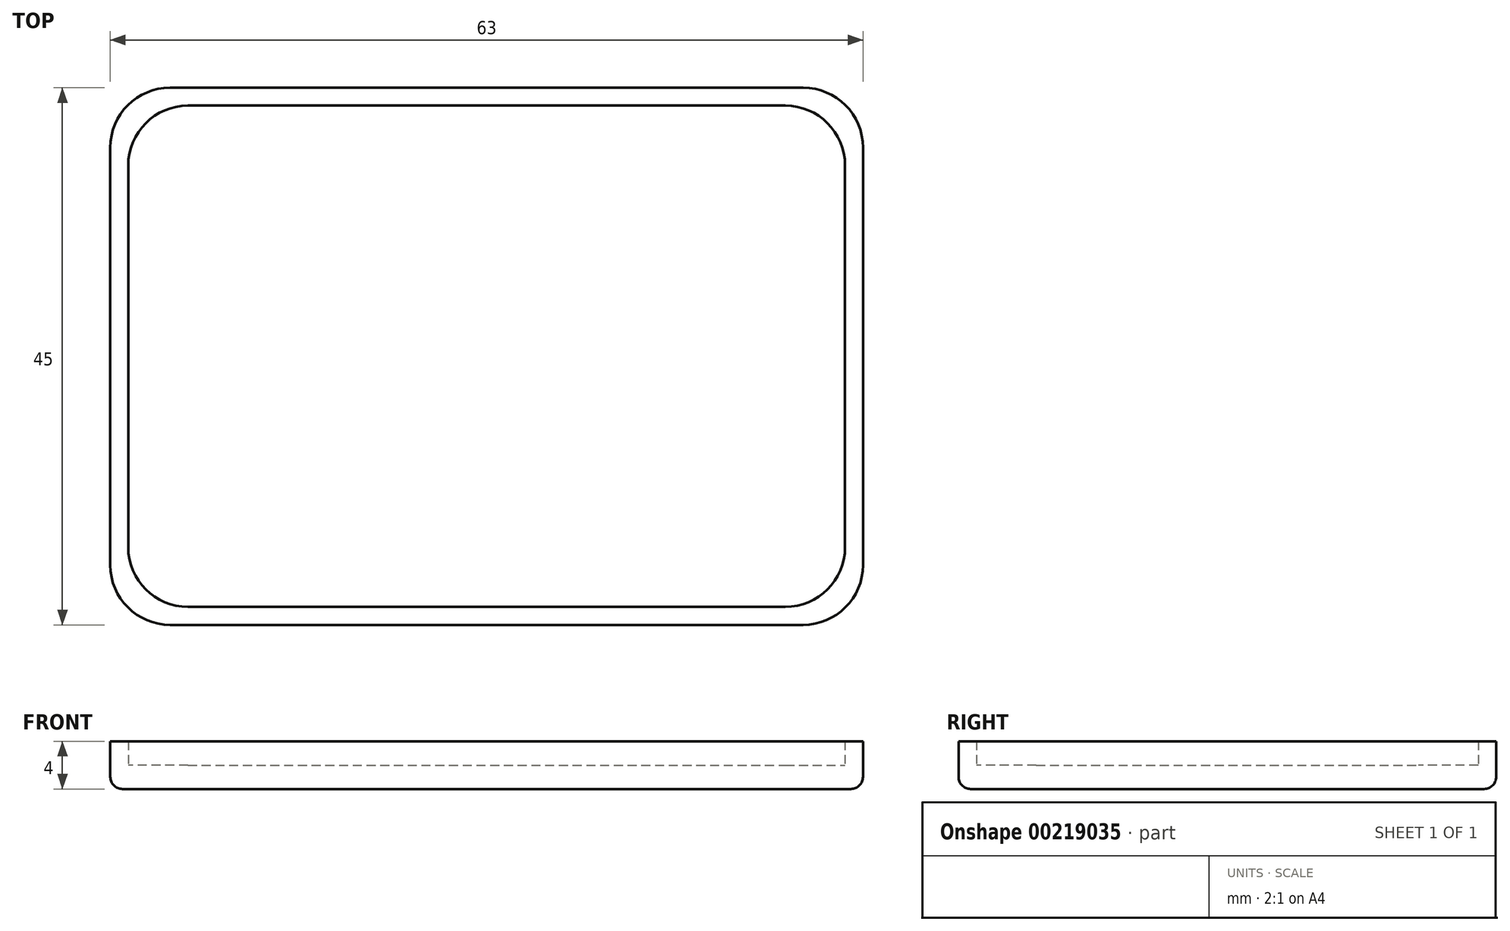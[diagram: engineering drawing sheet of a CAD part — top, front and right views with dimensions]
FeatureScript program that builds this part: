
annotation { "Feature Type Name" : "Feature", "Feature Type Description" : "" }
export const myFeature = defineFeature(function(context is Context, id is Id, definition is map)
    precondition{}
    {
        {
            var Q0;
            Q0=qCreatedBy(makeId("Top.planeOp"),FACE);
            var sketch = newSketch(context, id + "F0", { "sketchPlane" : qUnion([Q0])});
            skLineSegment(sketch, "E0.bottom", {"start": v(0, 0) * mm, "end": v(60, 0) * mm});
            skLineSegment(sketch, "E0.top", {"start": v(0, 42) * mm, "end": v(60, 42) * mm});
            skLineSegment(sketch, "E0.left", {"start": v(0, 0) * mm, "end": v(0, 42) * mm});
            skLineSegment(sketch, "E0.right", {"start": v(60, 0) * mm, "end": v(60, 42) * mm});
            skSolve(sketch);
        }
        {
            var Q0;
            Q0=qSketchRegion(id+"F0",true);
            extrude(context, id + "F1", {"entities" : qUnion([Q0]), "depth" : 2 * mm});
        }
        {
            var Q0;
            Q0=qCreatedBy(makeId("Top.planeOp"),FACE);
            var sketch = newSketch(context, id + "F2", { "sketchPlane" : qUnion([Q0])});
            skLineSegment(sketch, "E1.bottom", {"start": v(-1.5, 43.5) * mm, "end": v(61.5, 43.5) * mm});
            skLineSegment(sketch, "E1.top", {"start": v(-1.5, -1.5) * mm, "end": v(61.5, -1.5) * mm});
            skLineSegment(sketch, "E1.left", {"start": v(-1.5, 43.5) * mm, "end": v(-1.5, -1.5) * mm});
            skLineSegment(sketch, "E1.right", {"start": v(61.5, 43.5) * mm, "end": v(61.5, -1.5) * mm});
            skLineSegment(sketch, "E2.bottom", {"start": v(0, 42) * mm, "end": v(60, 42) * mm});
            skLineSegment(sketch, "E2.top", {"start": v(0, 0) * mm, "end": v(60, 0) * mm});
            skLineSegment(sketch, "E2.left", {"start": v(0, 42) * mm, "end": v(0, 0) * mm});
            skLineSegment(sketch, "E2.right", {"start": v(60, 42) * mm, "end": v(60, 0) * mm});
            skLineSegment(sketch, "E3", {"start": v(30, 42) * mm, "end": v(30, 43.5) * mm, "construction": true});
            skLineSegment(sketch, "E4", {"start": v(0, 21) * mm, "end": v(-1.5, 21) * mm, "construction": true});
            skSolve(sketch);
        }
        {
            var Q0;
            Q0=qSketchRegion(id+"F2",true);
            var Q1;
            Q1=qConstructionFilter(qBodyType(qCreatedBy(id+"F2",EDGE),BodyType.WIRE),ConstructionObject.NO);
            extrude(context, id + "F3", {"entities" : qUnion([Q0]), "operationType" : NewBodyOperationType.ADD, "surfaceEntities" : qUnion([Q1]), "depth" : 4 * mm});
        }
        {
            var Q0;
            Q0=makeQuery(id+"F3.opExtrude","SWEPT_EDGE",EDGE,{"disambiguationData":[OSD([sQuery(id+"F2.wireOp",EDGE,"E1.top"),sQuery(id+"F2.wireOp",EDGE,"E1.left")])]});
            var Q1;
            Q1=makeQuery(id+"F3.opExtrude","SWEPT_EDGE",EDGE,{"disambiguationData":[OSD([sQuery(id+"F2.wireOp",EDGE,"E1.top"),sQuery(id+"F2.wireOp",EDGE,"E1.right")])]});
            var Q2;
            Q2=makeQuery(id+"F3.opExtrude","SWEPT_EDGE",EDGE,{"disambiguationData":[OSD([sQuery(id+"F2.wireOp",EDGE,"E1.bottom"),sQuery(id+"F2.wireOp",EDGE,"E1.left")])]});
            var Q3;
            Q3=makeQuery(id+"F3.opExtrude","SWEPT_EDGE",EDGE,{"disambiguationData":[OSD([sQuery(id+"F2.wireOp",EDGE,"E2.bottom"),sQuery(id+"F2.wireOp",EDGE,"E2.right")])]});
            var Q4;
            Q4=makeQuery(id+"F3.opExtrude","SWEPT_EDGE",EDGE,{"disambiguationData":[OSD([sQuery(id+"F2.wireOp",EDGE,"E1.bottom"),sQuery(id+"F2.wireOp",EDGE,"E1.right")])]});
            var Q5;
            Q5=makeQuery(id+"F3.opExtrude","SWEPT_EDGE",EDGE,{"disambiguationData":[OSD([sQuery(id+"F2.wireOp",EDGE,"E2.top"),sQuery(id+"F2.wireOp",EDGE,"E2.right")])]});
            var Q6;
            Q6=makeQuery(id+"F3.opExtrude","SWEPT_EDGE",EDGE,{"disambiguationData":[OSD([sQuery(id+"F2.wireOp",EDGE,"E2.top"),sQuery(id+"F2.wireOp",EDGE,"E2.left")])]});
            var Q7;
            Q7=makeQuery(id+"F3.opExtrude","SWEPT_EDGE",EDGE,{"disambiguationData":[OSD([sQuery(id+"F2.wireOp",EDGE,"E2.bottom"),sQuery(id+"F2.wireOp",EDGE,"E2.left")])]});
            fillet(context, id + "F4", {"entities" : qUnion([Q0, Q1, Q2, Q3, Q4, Q5, Q6, Q7]), "radius" : 5 * mm, "tangentPropagation" : true, "allowEdgeOverflow" : false});
        }
        {
            var Q0;
            Q0=makeQuery(id+"F3.opExtrude","CAP_EDGE",EDGE,{"disambiguationData":[OSD([sQuery(id+"F2.wireOp",EDGE,"E1.top")])],"isStart":true});
            var Q1;
            {var subQ0=sQuery(id+"F2.wireOp",EDGE,"E1.right");var subQ1=sQuery(id+"F2.wireOp",EDGE,"E1.top");Q1=makeQuery(id+"F4.opFillet","BLEND_EDGE",EDGE,{"blendedFrom":[makeQuery(id+"F3.opExtrude","SWEPT_EDGE",EDGE,{"disambiguationData":[OSD([subQ1,subQ0])]}),makeQuery(id+"F3.boolean.opBoolean","MERGE",FACE,{"derivedFrom":[makeQuery(id+"F1.opExtrude","CAP_FACE",FACE,{"disambiguationData":[OSD([sQuery(id+"F0.wireOp",EDGE,"E0.bottom"),sQuery(id+"F0.wireOp",EDGE,"E0.top"),sQuery(id+"F0.wireOp",EDGE,"E0.left"),sQuery(id+"F0.wireOp",EDGE,"E0.right")])],"isStart":true}),makeQuery(id+"F3.opExtrude","CAP_FACE",FACE,{"disambiguationData":[OSD([sQuery(id+"F2.wireOp",EDGE,"E1.bottom"),subQ1,sQuery(id+"F2.wireOp",EDGE,"E1.left"),subQ0,sQuery(id+"F2.wireOp",EDGE,"E2.bottom"),sQuery(id+"F2.wireOp",EDGE,"E2.top"),sQuery(id+"F2.wireOp",EDGE,"E2.left"),sQuery(id+"F2.wireOp",EDGE,"E2.right")])],"isStart":true})]})],"blendedInto":[makeQuery(id+"F3.boolean.opBoolean","MERGE",FACE,{"derivedFrom":[makeQuery(id+"F1.opExtrude","CAP_FACE",FACE,{"disambiguationData":[OSD([sQuery(id+"F0.wireOp",EDGE,"E0.bottom"),sQuery(id+"F0.wireOp",EDGE,"E0.top"),sQuery(id+"F0.wireOp",EDGE,"E0.left"),sQuery(id+"F0.wireOp",EDGE,"E0.right")])],"isStart":true}),makeQuery(id+"F3.opExtrude","CAP_FACE",FACE,{"disambiguationData":[OSD([sQuery(id+"F2.wireOp",EDGE,"E1.bottom"),subQ1,sQuery(id+"F2.wireOp",EDGE,"E1.left"),subQ0,sQuery(id+"F2.wireOp",EDGE,"E2.bottom"),sQuery(id+"F2.wireOp",EDGE,"E2.top"),sQuery(id+"F2.wireOp",EDGE,"E2.left"),sQuery(id+"F2.wireOp",EDGE,"E2.right")])],"isStart":true})]})]});}
            var Q2;
            Q2=makeQuery(id+"F3.opExtrude","CAP_EDGE",EDGE,{"disambiguationData":[OSD([sQuery(id+"F2.wireOp",EDGE,"E1.right")])],"isStart":true});
            var Q3;
            {var subQ0=sQuery(id+"F2.wireOp",EDGE,"E1.right");var subQ1=sQuery(id+"F2.wireOp",EDGE,"E1.bottom");Q3=makeQuery(id+"F4.opFillet","BLEND_EDGE",EDGE,{"blendedFrom":[makeQuery(id+"F3.opExtrude","SWEPT_EDGE",EDGE,{"disambiguationData":[OSD([subQ1,subQ0])]}),makeQuery(id+"F3.boolean.opBoolean","MERGE",FACE,{"derivedFrom":[makeQuery(id+"F1.opExtrude","CAP_FACE",FACE,{"disambiguationData":[OSD([sQuery(id+"F0.wireOp",EDGE,"E0.bottom"),sQuery(id+"F0.wireOp",EDGE,"E0.top"),sQuery(id+"F0.wireOp",EDGE,"E0.left"),sQuery(id+"F0.wireOp",EDGE,"E0.right")])],"isStart":true}),makeQuery(id+"F3.opExtrude","CAP_FACE",FACE,{"disambiguationData":[OSD([subQ1,sQuery(id+"F2.wireOp",EDGE,"E1.top"),sQuery(id+"F2.wireOp",EDGE,"E1.left"),subQ0,sQuery(id+"F2.wireOp",EDGE,"E2.bottom"),sQuery(id+"F2.wireOp",EDGE,"E2.top"),sQuery(id+"F2.wireOp",EDGE,"E2.left"),sQuery(id+"F2.wireOp",EDGE,"E2.right")])],"isStart":true})]})],"blendedInto":[makeQuery(id+"F3.boolean.opBoolean","MERGE",FACE,{"derivedFrom":[makeQuery(id+"F1.opExtrude","CAP_FACE",FACE,{"disambiguationData":[OSD([sQuery(id+"F0.wireOp",EDGE,"E0.bottom"),sQuery(id+"F0.wireOp",EDGE,"E0.top"),sQuery(id+"F0.wireOp",EDGE,"E0.left"),sQuery(id+"F0.wireOp",EDGE,"E0.right")])],"isStart":true}),makeQuery(id+"F3.opExtrude","CAP_FACE",FACE,{"disambiguationData":[OSD([subQ1,sQuery(id+"F2.wireOp",EDGE,"E1.top"),sQuery(id+"F2.wireOp",EDGE,"E1.left"),subQ0,sQuery(id+"F2.wireOp",EDGE,"E2.bottom"),sQuery(id+"F2.wireOp",EDGE,"E2.top"),sQuery(id+"F2.wireOp",EDGE,"E2.left"),sQuery(id+"F2.wireOp",EDGE,"E2.right")])],"isStart":true})]})]});}
            var Q4;
            Q4=makeQuery(id+"F3.opExtrude","CAP_EDGE",EDGE,{"disambiguationData":[OSD([sQuery(id+"F2.wireOp",EDGE,"E1.bottom")])],"isStart":true});
            var Q5;
            {var subQ0=sQuery(id+"F2.wireOp",EDGE,"E1.left");var subQ1=sQuery(id+"F2.wireOp",EDGE,"E1.bottom");Q5=makeQuery(id+"F4.opFillet","BLEND_EDGE",EDGE,{"blendedFrom":[makeQuery(id+"F3.opExtrude","SWEPT_EDGE",EDGE,{"disambiguationData":[OSD([subQ1,subQ0])]}),makeQuery(id+"F3.boolean.opBoolean","MERGE",FACE,{"derivedFrom":[makeQuery(id+"F1.opExtrude","CAP_FACE",FACE,{"disambiguationData":[OSD([sQuery(id+"F0.wireOp",EDGE,"E0.bottom"),sQuery(id+"F0.wireOp",EDGE,"E0.top"),sQuery(id+"F0.wireOp",EDGE,"E0.left"),sQuery(id+"F0.wireOp",EDGE,"E0.right")])],"isStart":true}),makeQuery(id+"F3.opExtrude","CAP_FACE",FACE,{"disambiguationData":[OSD([subQ1,sQuery(id+"F2.wireOp",EDGE,"E1.top"),subQ0,sQuery(id+"F2.wireOp",EDGE,"E1.right"),sQuery(id+"F2.wireOp",EDGE,"E2.bottom"),sQuery(id+"F2.wireOp",EDGE,"E2.top"),sQuery(id+"F2.wireOp",EDGE,"E2.left"),sQuery(id+"F2.wireOp",EDGE,"E2.right")])],"isStart":true})]})],"blendedInto":[makeQuery(id+"F3.boolean.opBoolean","MERGE",FACE,{"derivedFrom":[makeQuery(id+"F1.opExtrude","CAP_FACE",FACE,{"disambiguationData":[OSD([sQuery(id+"F0.wireOp",EDGE,"E0.bottom"),sQuery(id+"F0.wireOp",EDGE,"E0.top"),sQuery(id+"F0.wireOp",EDGE,"E0.left"),sQuery(id+"F0.wireOp",EDGE,"E0.right")])],"isStart":true}),makeQuery(id+"F3.opExtrude","CAP_FACE",FACE,{"disambiguationData":[OSD([subQ1,sQuery(id+"F2.wireOp",EDGE,"E1.top"),subQ0,sQuery(id+"F2.wireOp",EDGE,"E1.right"),sQuery(id+"F2.wireOp",EDGE,"E2.bottom"),sQuery(id+"F2.wireOp",EDGE,"E2.top"),sQuery(id+"F2.wireOp",EDGE,"E2.left"),sQuery(id+"F2.wireOp",EDGE,"E2.right")])],"isStart":true})]})]});}
            var Q6;
            Q6=makeQuery(id+"F3.opExtrude","CAP_EDGE",EDGE,{"disambiguationData":[OSD([sQuery(id+"F2.wireOp",EDGE,"E1.left")])],"isStart":true});
            var Q7;
            {var subQ0=sQuery(id+"F2.wireOp",EDGE,"E1.left");var subQ1=sQuery(id+"F2.wireOp",EDGE,"E1.top");Q7=makeQuery(id+"F4.opFillet","BLEND_EDGE",EDGE,{"blendedFrom":[makeQuery(id+"F3.opExtrude","SWEPT_EDGE",EDGE,{"disambiguationData":[OSD([subQ1,subQ0])]}),makeQuery(id+"F3.boolean.opBoolean","MERGE",FACE,{"derivedFrom":[makeQuery(id+"F1.opExtrude","CAP_FACE",FACE,{"disambiguationData":[OSD([sQuery(id+"F0.wireOp",EDGE,"E0.bottom"),sQuery(id+"F0.wireOp",EDGE,"E0.top"),sQuery(id+"F0.wireOp",EDGE,"E0.left"),sQuery(id+"F0.wireOp",EDGE,"E0.right")])],"isStart":true}),makeQuery(id+"F3.opExtrude","CAP_FACE",FACE,{"disambiguationData":[OSD([sQuery(id+"F2.wireOp",EDGE,"E1.bottom"),subQ1,subQ0,sQuery(id+"F2.wireOp",EDGE,"E1.right"),sQuery(id+"F2.wireOp",EDGE,"E2.bottom"),sQuery(id+"F2.wireOp",EDGE,"E2.top"),sQuery(id+"F2.wireOp",EDGE,"E2.left"),sQuery(id+"F2.wireOp",EDGE,"E2.right")])],"isStart":true})]})],"blendedInto":[makeQuery(id+"F3.boolean.opBoolean","MERGE",FACE,{"derivedFrom":[makeQuery(id+"F1.opExtrude","CAP_FACE",FACE,{"disambiguationData":[OSD([sQuery(id+"F0.wireOp",EDGE,"E0.bottom"),sQuery(id+"F0.wireOp",EDGE,"E0.top"),sQuery(id+"F0.wireOp",EDGE,"E0.left"),sQuery(id+"F0.wireOp",EDGE,"E0.right")])],"isStart":true}),makeQuery(id+"F3.opExtrude","CAP_FACE",FACE,{"disambiguationData":[OSD([sQuery(id+"F2.wireOp",EDGE,"E1.bottom"),subQ1,subQ0,sQuery(id+"F2.wireOp",EDGE,"E1.right"),sQuery(id+"F2.wireOp",EDGE,"E2.bottom"),sQuery(id+"F2.wireOp",EDGE,"E2.top"),sQuery(id+"F2.wireOp",EDGE,"E2.left"),sQuery(id+"F2.wireOp",EDGE,"E2.right")])],"isStart":true})]})]});}
            fillet(context, id + "F5", {"entities" : qUnion([Q0, Q1, Q2, Q3, Q4, Q5, Q6, Q7]), "radius" : 1 * mm, "tangentPropagation" : true, "allowEdgeOverflow" : false});
        }
    });
